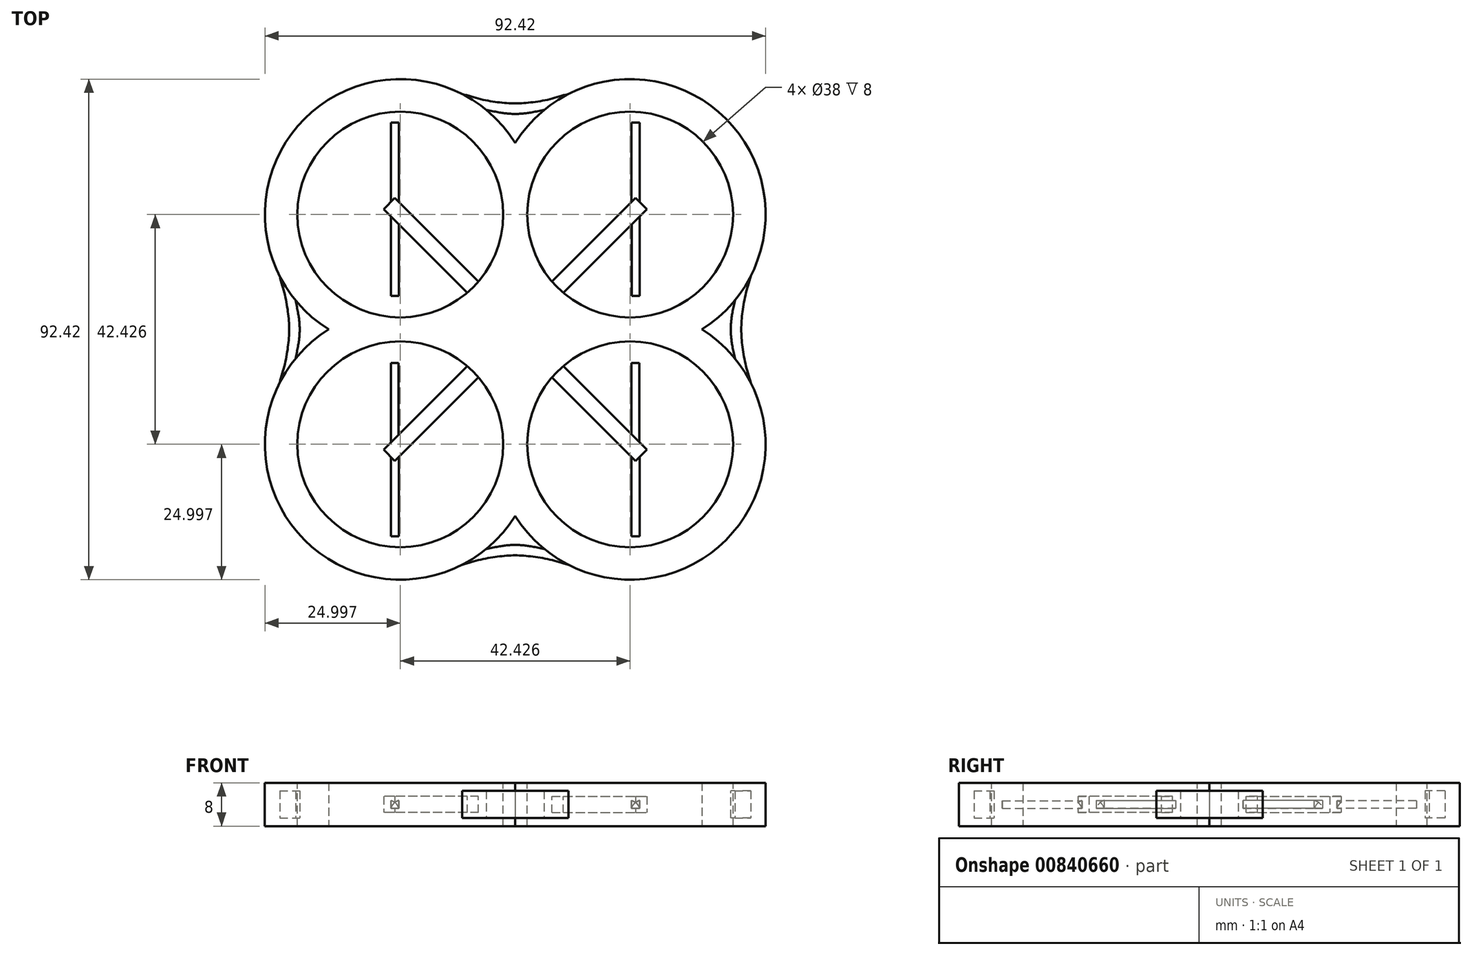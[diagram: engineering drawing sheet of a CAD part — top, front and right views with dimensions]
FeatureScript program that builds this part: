
annotation { "Feature Type Name" : "Feature", "Feature Type Description" : "" }
export const myFeature = defineFeature(function(context is Context, id is Id, definition is map)
    precondition{}
    {
        {
            var Q0;
            Q0=qCreatedBy(makeId("Top.planeOp"),FACE);
            var sketch = newSketch(context, id + "F0", { "sketchPlane" : qUnion([Q0])});
            skLineSegment(sketch, "E0", {"start": v(0, 0) * mm, "end": v(42.43, 42.43) * mm, "construction": true});
            skLineSegment(sketch, "E1", {"start": v(0, 0) * mm, "end": v(21.21, 21.21) * mm});
            skCircle(sketch, "E2", {"center": v(21.21, 21.21) * mm, "radius": 25 * mm});
            skCircle(sketch, "E3.MirrorC", {"center": v(21.21, -21.21) * mm, "radius": 25 * mm});
            skCircle(sketch, "E4.MirrorC", {"center": v(-21.21, 21.21) * mm, "radius": 25 * mm});
            skCircle(sketch, "E5.MirrorC", {"center": v(-21.21, -21.21) * mm, "radius": 25 * mm});
            skSolve(sketch);
        }
        {
            var Q0;
            Q0 = qSketchRegion(id + "F0", true);
            extrude(context, id + "F1", {"entities" : qUnion([Q0]), "endBound" : BoundingType.SYMMETRIC, "depth" : 8 * mm, "offsetDistance" : 25 * mm});
        }
        {
            var Q0;
            Q0=qCreatedBy(makeId("Top.planeOp"),FACE);
            var sketch = newSketch(context, id + "F2", { "sketchPlane" : qUnion([Q0])});
            skLineSegment(sketch, "E6", {"start": v(0, 0) * mm, "end": v(42.43, 42.43) * mm, "construction": true});
            skLineSegment(sketch, "E7", {"start": v(0, 0) * mm, "end": v(21.21, 21.21) * mm});
            skCircle(sketch, "E8", {"center": v(21.21, 21.21) * mm, "radius": 19 * mm});
            skCircle(sketch, "E9.MirrorC", {"center": v(-21.21, 21.21) * mm, "radius": 19 * mm});
            skCircle(sketch, "E10.MirrorC", {"center": v(21.21, -21.21) * mm, "radius": 19 * mm});
            skCircle(sketch, "E11.MirrorC", {"center": v(-21.21, -21.21) * mm, "radius": 19 * mm});
            skSolve(sketch);
        }
        {
            var Q0;
            Q0 = qSketchRegion(id + "F2", true);
            extrude(context, id + "F3", {"entities" : qUnion([Q0]), "operationType" : NewBodyOperationType.REMOVE, "endBound" : BoundingType.SYMMETRIC, "oppositeDirection" : true, "depth" : 25 * mm, "offsetDistance" : 25 * mm});
        }
        {
            var Q0;
            Q0=qCreatedBy(makeId("Top.planeOp"),FACE);
            var sketch = newSketch(context, id + "F4", { "sketchPlane" : qUnion([Q0])});
            skFitSpline(sketch, "E12", {"points": [v(-10.9, 43.62) * mm, v(-7.26, 42.73) * mm, v(-3.36, 41.97) * mm, v(0, 41.72) * mm], "startDerivative": vector(10.52, -0.67) * mm, "endDerivative": vector(9.64, 0) * mm});
            skFitSpline(sketch, "E13", {"points": [v(-6.55, 40.73) * mm, v(-3.36, 40.14) * mm, v(-1.56, 39.87) * mm, v(0, 39.8) * mm], "startDerivative": vector(8.27, -1.19) * mm, "endDerivative": vector(5.4, 0.03) * mm});
            skLineSegment(sketch, "E14", {"start": v(0, 0) * mm, "end": v(31.64, 31.64) * mm, "construction": true});
            skFitSpline(sketch, "E15.MirrorCS", {"points": [v(43.62, -10.9) * mm, v(42.73, -7.26) * mm, v(41.97, -3.36) * mm, v(41.72, 0) * mm], "startDerivative": vector(-0.67, 10.52) * mm, "endDerivative": vector(0, 9.64) * mm});
            skFitSpline(sketch, "E16.MirrorCS", {"points": [v(40.73, -6.55) * mm, v(40.14, -3.36) * mm, v(39.87, -1.56) * mm, v(39.8, 0) * mm], "startDerivative": vector(-1.19, 8.27) * mm, "endDerivative": vector(0.03, 5.4) * mm});
            skFitSpline(sketch, "E17.MirrorCS", {"points": [v(10.9, 43.62) * mm, v(7.26, 42.73) * mm, v(3.36, 41.97) * mm, v(0, 41.72) * mm], "startDerivative": vector(-10.52, -0.67) * mm, "endDerivative": vector(-9.64, 0) * mm});
            skFitSpline(sketch, "E18.MirrorCS", {"points": [v(6.55, 40.73) * mm, v(3.36, 40.14) * mm, v(1.56, 39.87) * mm, v(0, 39.8) * mm], "startDerivative": vector(-8.27, -1.19) * mm, "endDerivative": vector(-5.4, 0.03) * mm});
            skFitSpline(sketch, "E19.MirrorCS", {"points": [v(-43.62, -10.9) * mm, v(-42.73, -7.26) * mm, v(-41.97, -3.36) * mm, v(-41.72, 0) * mm], "startDerivative": vector(0.67, 10.52) * mm, "endDerivative": vector(0, 9.64) * mm});
            skFitSpline(sketch, "E20.MirrorCS", {"points": [v(-40.73, -6.55) * mm, v(-40.14, -3.36) * mm, v(-39.87, -1.56) * mm, v(-39.8, 0) * mm], "startDerivative": vector(1.19, 8.27) * mm, "endDerivative": vector(-0.03, 5.4) * mm});
            skFitSpline(sketch, "E21.MirrorCS", {"points": [v(43.62, 10.9) * mm, v(42.73, 7.26) * mm, v(41.97, 3.36) * mm, v(41.72, 0) * mm], "startDerivative": vector(-0.67, -10.52) * mm, "endDerivative": vector(0, -9.64) * mm});
            skFitSpline(sketch, "E22.MirrorCS", {"points": [v(40.73, 6.55) * mm, v(40.14, 3.36) * mm, v(39.87, 1.56) * mm, v(39.8, 0) * mm], "startDerivative": vector(-1.19, -8.27) * mm, "endDerivative": vector(0.03, -5.4) * mm});
            skFitSpline(sketch, "E23.MirrorCS", {"points": [v(10.9, -43.62) * mm, v(7.26, -42.73) * mm, v(3.36, -41.97) * mm, v(0, -41.72) * mm], "startDerivative": vector(-10.52, 0.67) * mm, "endDerivative": vector(-9.64, 0) * mm});
            skFitSpline(sketch, "E24.MirrorCS", {"points": [v(6.55, -40.73) * mm, v(3.36, -40.14) * mm, v(1.56, -39.87) * mm, v(0, -39.8) * mm], "startDerivative": vector(-8.27, 1.19) * mm, "endDerivative": vector(-5.4, -0.03) * mm});
            skFitSpline(sketch, "E25.MirrorCS", {"points": [v(-10.9, -43.62) * mm, v(-7.26, -42.73) * mm, v(-3.36, -41.97) * mm, v(0, -41.72) * mm], "startDerivative": vector(10.52, 0.67) * mm, "endDerivative": vector(9.64, 0) * mm});
            skFitSpline(sketch, "E26.MirrorCS", {"points": [v(-6.55, -40.73) * mm, v(-3.36, -40.14) * mm, v(-1.56, -39.87) * mm, v(0, -39.8) * mm], "startDerivative": vector(8.27, 1.19) * mm, "endDerivative": vector(5.4, -0.03) * mm});
            skFitSpline(sketch, "E27.MirrorCS", {"points": [v(-40.73, 6.55) * mm, v(-40.14, 3.36) * mm, v(-39.87, 1.56) * mm, v(-39.8, 0) * mm], "startDerivative": vector(1.19, -8.27) * mm, "endDerivative": vector(-0.03, -5.4) * mm});
            skFitSpline(sketch, "E28.MirrorCS", {"points": [v(-43.62, 10.9) * mm, v(-42.73, 7.26) * mm, v(-41.97, 3.36) * mm, v(-41.72, 0) * mm], "startDerivative": vector(0.67, -10.52) * mm, "endDerivative": vector(0, -9.64) * mm});
            skLineSegment(sketch, "E29", {"start": v(-43.62, 10.9) * mm, "end": v(-40.73, 6.55) * mm});
            skLineSegment(sketch, "E30", {"start": v(-40.73, -6.55) * mm, "end": v(-43.62, -10.9) * mm});
            skLineSegment(sketch, "E31", {"start": v(-10.9, 43.62) * mm, "end": v(-6.55, 40.73) * mm});
            skLineSegment(sketch, "E32", {"start": v(10.9, 43.62) * mm, "end": v(6.55, 40.73) * mm});
            skLineSegment(sketch, "E33", {"start": v(-6.55, -40.73) * mm, "end": v(-10.9, -43.62) * mm});
            skLineSegment(sketch, "E34", {"start": v(6.55, -40.73) * mm, "end": v(10.9, -43.62) * mm});
            skLineSegment(sketch, "E35", {"start": v(43.62, -10.9) * mm, "end": v(40.73, -6.55) * mm});
            skLineSegment(sketch, "E36", {"start": v(43.62, 10.9) * mm, "end": v(40.73, 6.55) * mm});
            skSolve(sketch);
        }
        {
            var Q0;
            Q0 = qSketchRegion(id + "F4", true);
            extrude(context, id + "F5", {"entities" : qUnion([Q0]), "operationType" : NewBodyOperationType.ADD, "endBound" : BoundingType.SYMMETRIC, "depth" : 5 * mm, "offsetDistance" : 25 * mm});
        }
        {
            var Q0;
            Q0=qCreatedBy(makeId("Top.planeOp"),FACE);
            var sketch = newSketch(context, id + "F6", { "sketchPlane" : qUnion([Q0])});
            skFitSpline(sketch, "E37", {"points": [v(0, 21.62) * mm, v(-3.08, 14.95) * mm, v(-6.05, 8.7) * mm, v(-9.09, 0) * mm], "startDerivative": vector(-14.1, -3.44) * mm, "endDerivative": vector(-1.81, -25) * mm});
            skFitSpline(sketch, "E38.MirrorCS", {"points": [v(0, 21.62) * mm, v(3.08, 14.95) * mm, v(6.05, 8.7) * mm, v(9.09, 0) * mm], "startDerivative": vector(14.1, -3.44) * mm, "endDerivative": vector(1.81, -25) * mm});
            skFitSpline(sketch, "E39.MirrorCS", {"points": [v(0, -21.62) * mm, v(-3.08, -14.95) * mm, v(-6.05, -8.7) * mm, v(-9.09, 0) * mm], "startDerivative": vector(-14.1, 3.44) * mm, "endDerivative": vector(-1.81, 25) * mm});
            skFitSpline(sketch, "E40.MirrorCS", {"points": [v(0, -21.62) * mm, v(3.08, -14.95) * mm, v(6.05, -8.7) * mm, v(9.09, 0) * mm], "startDerivative": vector(14.1, 3.44) * mm, "endDerivative": vector(1.81, 25) * mm});
            skSolve(sketch);
        }
        {
            var Q0;
            Q0 = qSketchRegion(id + "F6", true);
            extrude(context, id + "F7", {"entities" : qUnion([Q0]), "operationType" : NewBodyOperationType.ADD, "endBound" : BoundingType.SYMMETRIC, "depth" : 8 * mm, "offsetDistance" : 25 * mm});
        }
        {
            var Q0;
            Q0=qCreatedBy(makeId("Top.planeOp"),FACE);
            var sketch = newSketch(context, id + "F8", { "sketchPlane" : qUnion([Q0])});
            skLineSegment(sketch, "E41", {"start": v(-2.07, 0) * mm, "end": v(-23.29, 21.21) * mm});
            skLineSegment(sketch, "E42", {"start": v(0, 0) * mm, "end": v(-42.43, 42.43) * mm, "construction": true});
            skLineSegment(sketch, "E43.MirrorCS", {"start": v(0, 2.07) * mm, "end": v(-21.21, 23.29) * mm});
            skLineSegment(sketch, "E44.MirrorCS", {"start": v(0, 2.07) * mm, "end": v(21.21, 23.29) * mm});
            skLineSegment(sketch, "E45.MirrorCS", {"start": v(2.07, 0) * mm, "end": v(23.29, 21.21) * mm});
            skLineSegment(sketch, "E46.MirrorCS", {"start": v(2.07, 0) * mm, "end": v(23.29, -21.21) * mm});
            skLineSegment(sketch, "E47.MirrorCS", {"start": v(0, -2.07) * mm, "end": v(21.21, -23.29) * mm});
            skLineSegment(sketch, "E48.MirrorCS", {"start": v(-2.07, 0) * mm, "end": v(-23.29, -21.21) * mm});
            skLineSegment(sketch, "E49.MirrorCS", {"start": v(0, -2.07) * mm, "end": v(-21.21, -23.29) * mm});
            skLineSegment(sketch, "E50", {"start": v(2.07, 0) * mm, "end": v(23.21, 21.14) * mm});
            skLineSegment(sketch, "E51", {"start": v(21.21, 23.29) * mm, "end": v(23.21, 21.14) * mm});
            skLineSegment(sketch, "E52.MirrorCS", {"start": v(-21.21, 23.29) * mm, "end": v(-23.21, 21.14) * mm});
            skLineSegment(sketch, "E53.MirrorCS", {"start": v(0, 0) * mm, "end": v(-42.43, -42.43) * mm, "construction": true});
            skLineSegment(sketch, "E54.MirrorCS", {"start": v(-21.21, -23.29) * mm, "end": v(-23.21, -21.14) * mm});
            skLineSegment(sketch, "E55.MirrorCS", {"start": v(21.21, -23.29) * mm, "end": v(23.21, -21.14) * mm});
            skLineSegment(sketch, "E56", {"start": v(23.21, -21.14) * mm, "end": v(21.21, -23.29) * mm});
            skLineSegment(sketch, "E57", {"start": v(-23.21, -21.14) * mm, "end": v(-21.21, -23.29) * mm});
            skLineSegment(sketch, "E58", {"start": v(0, 2.07) * mm, "end": v(-22.21, 24.29) * mm});
            skPoint(sketch, "E58.endSnap0", {"position": v(-22.21, 22.21) * mm});
            skLineSegment(sketch, "E59.MirrorCS", {"start": v(-2.07, 0) * mm, "end": v(-24.29, 22.21) * mm});
            skLineSegment(sketch, "E60.MirrorCS", {"start": v(0, 2.07) * mm, "end": v(22.21, 24.29) * mm});
            skLineSegment(sketch, "E61.MirrorCS", {"start": v(2.07, 0) * mm, "end": v(24.29, 22.21) * mm});
            skLineSegment(sketch, "E62.MirrorCS", {"start": v(0, -2.07) * mm, "end": v(-22.21, -24.29) * mm});
            skLineSegment(sketch, "E63.MirrorCS", {"start": v(-2.07, 0) * mm, "end": v(-24.29, -22.21) * mm});
            skLineSegment(sketch, "E64.MirrorCS", {"start": v(2.07, 0) * mm, "end": v(24.29, -22.21) * mm});
            skLineSegment(sketch, "E65.MirrorCS", {"start": v(0, -2.07) * mm, "end": v(22.21, -24.29) * mm});
            skLineSegment(sketch, "E66", {"start": v(0, 2.07) * mm, "end": v(-20.14, 22.21) * mm});
            skLineSegment(sketch, "E67", {"start": v(-20.14, 22.21) * mm, "end": v(-22.21, 20.14) * mm});
            skLineSegment(sketch, "E68", {"start": v(-22.21, 20.14) * mm, "end": v(-22.21, 24.29) * mm});
            skLineSegment(sketch, "E69", {"start": v(-22.21, 24.29) * mm, "end": v(-24.29, 22.21) * mm});
            skLineSegment(sketch, "E70", {"start": v(-24.29, 22.21) * mm, "end": v(-20.14, 22.21) * mm});
            skLineSegment(sketch, "E71.MirrorCS", {"start": v(22.21, 24.29) * mm, "end": v(24.29, 22.21) * mm});
            skLineSegment(sketch, "E72.MirrorCS", {"start": v(20.14, 22.21) * mm, "end": v(22.21, 20.14) * mm});
            skLineSegment(sketch, "E73.MirrorCS", {"start": v(22.21, 20.14) * mm, "end": v(22.21, 24.29) * mm});
            skLineSegment(sketch, "E74.MirrorCS", {"start": v(24.29, 22.21) * mm, "end": v(20.14, 22.21) * mm});
            skPoint(sketch, "E75", {"position": v(22.21, 22.21) * mm});
            skLineSegment(sketch, "E76.MirrorCS", {"start": v(22.21, -20.14) * mm, "end": v(22.21, -24.29) * mm});
            skLineSegment(sketch, "E77.MirrorCS", {"start": v(24.29, -22.21) * mm, "end": v(20.14, -22.21) * mm});
            skPoint(sketch, "E78.MirrorP", {"position": v(22.21, -22.21) * mm});
            skLineSegment(sketch, "E79.MirrorCS", {"start": v(22.21, -24.29) * mm, "end": v(24.29, -22.21) * mm});
            skLineSegment(sketch, "E80.MirrorCS", {"start": v(20.14, -22.21) * mm, "end": v(22.21, -20.14) * mm});
            skLineSegment(sketch, "E81.MirrorCS", {"start": v(-20.14, -22.21) * mm, "end": v(-22.21, -20.14) * mm});
            skLineSegment(sketch, "E82.MirrorCS", {"start": v(-22.21, -24.29) * mm, "end": v(-24.29, -22.21) * mm});
            skLineSegment(sketch, "E83.MirrorCS", {"start": v(-24.29, -22.21) * mm, "end": v(-20.14, -22.21) * mm});
            skLineSegment(sketch, "E84.MirrorCS", {"start": v(-22.21, -20.14) * mm, "end": v(-22.21, -24.29) * mm});
            skPoint(sketch, "E85.MirrorP", {"position": v(-22.21, -22.21) * mm});
            skSolve(sketch);
        }
        {
            var Q0;
            Q0 = qSketchRegion(id + "F8", true);
            extrude(context, id + "F9", {"entities" : qUnion([Q0]), "operationType" : NewBodyOperationType.ADD, "endBound" : BoundingType.SYMMETRIC, "depth" : 3 * mm, "offsetDistance" : 25 * mm});
        }
        {
            var Q0;
            Q0=qCreatedBy(makeId("Top.planeOp"),FACE);
            var sketch = newSketch(context, id + "F10", { "sketchPlane" : qUnion([Q0])});
            skLineSegment(sketch, "E86.bottom", {"start": v(-22.96, 38.21) * mm, "end": v(-21.46, 38.21) * mm});
            skLineSegment(sketch, "E86.top", {"start": v(-22.96, 6.21) * mm, "end": v(-21.46, 6.21) * mm});
            skLineSegment(sketch, "E86.left", {"start": v(-22.96, 38.21) * mm, "end": v(-22.96, 6.21) * mm});
            skLineSegment(sketch, "E86.right", {"start": v(-21.46, 38.21) * mm, "end": v(-21.46, 6.21) * mm});
            skPoint(sketch, "E86.middle", {"position": v(-22.21, 22.21) * mm});
            skLineSegment(sketch, "E87.MirrorCS", {"start": v(21.46, 38.21) * mm, "end": v(21.46, 6.21) * mm});
            skLineSegment(sketch, "E88.MirrorCS", {"start": v(22.96, 38.21) * mm, "end": v(22.96, 6.21) * mm});
            skLineSegment(sketch, "E89.MirrorCS", {"start": v(22.96, 38.21) * mm, "end": v(21.46, 38.21) * mm});
            skLineSegment(sketch, "E90.MirrorCS", {"start": v(22.96, 6.21) * mm, "end": v(21.46, 6.21) * mm});
            skLineSegment(sketch, "E91.MirrorCS", {"start": v(-22.96, -38.21) * mm, "end": v(-22.96, -6.21) * mm});
            skLineSegment(sketch, "E92.MirrorCS", {"start": v(-21.46, -38.21) * mm, "end": v(-21.46, -6.21) * mm});
            skLineSegment(sketch, "E93.MirrorCS", {"start": v(-22.96, -6.21) * mm, "end": v(-21.46, -6.21) * mm});
            skLineSegment(sketch, "E94.MirrorCS", {"start": v(-22.96, -38.21) * mm, "end": v(-21.46, -38.21) * mm});
            skLineSegment(sketch, "E95.MirrorCS", {"start": v(22.96, -38.21) * mm, "end": v(21.46, -38.21) * mm});
            skLineSegment(sketch, "E96.MirrorCS", {"start": v(22.96, -6.21) * mm, "end": v(21.46, -6.21) * mm});
            skLineSegment(sketch, "E97.MirrorCS", {"start": v(21.46, -38.21) * mm, "end": v(21.46, -6.21) * mm});
            skLineSegment(sketch, "E98.MirrorCS", {"start": v(22.96, -38.21) * mm, "end": v(22.96, -6.21) * mm});
            skSolve(sketch);
        }
        {
            var Q0;
            Q0 = qSketchRegion(id + "F10", true);
            extrude(context, id + "F11", {"entities" : qUnion([Q0]), "operationType" : NewBodyOperationType.ADD, "endBound" : BoundingType.SYMMETRIC, "depth" : 1.5 * mm, "offsetDistance" : 25 * mm});
        }
        {
            var Q0;
            {var subQ1=sQuery(id+"F10.wireOp",EDGE,"E88.MirrorCS");Q0=makeQuery(id+"F11.boolean.opBoolean","SPLIT",EDGE,{"disambiguationData":[TD([makeQuery(id+"F9.opExtrude","SWEPT_FACE",FACE,{"disambiguationData":[OSD([sQuery(id+"F8.wireOp",EDGE,"E71.MirrorCS")])]})])],"derivedFrom":makeQuery(id+"F11.opExtrude","CAP_EDGE",EDGE,{"disambiguationData":[OSD([subQ1])],"isStart":false})});}
            var Q1;
            {var subQ0=sQuery(id+"F10.wireOp",EDGE,"E87.MirrorCS");Q1=makeQuery(id+"F11.boolean.opBoolean","SPLIT",EDGE,{"disambiguationData":[TD([makeQuery(id+"F9.opExtrude","SWEPT_FACE",FACE,{"disambiguationData":[OSD([sQuery(id+"F8.wireOp",EDGE,"E61.MirrorCS")])]})])],"derivedFrom":makeQuery(id+"F11.opExtrude","CAP_EDGE",EDGE,{"disambiguationData":[OSD([subQ0])],"isStart":false})});}
            var Q2;
            {var subQ0=sQuery(id+"F10.wireOp",EDGE,"E86.bottom");var subQ1=sQuery(id+"F10.wireOp",EDGE,"E86.right");Q2=makeQuery(id+"F11.boolean.opBoolean","SPLIT",EDGE,{"disambiguationData":[TD([makeQuery(id+"F11.opExtrude","SWEPT_FACE",FACE,{"disambiguationData":[OSD([subQ0])]})])],"derivedFrom":makeQuery(id+"F11.opExtrude","CAP_EDGE",EDGE,{"disambiguationData":[OSD([subQ1])],"isStart":false})});}
            var Q3;
            {var subQ0=sQuery(id+"F10.wireOp",EDGE,"E86.left");Q3=makeQuery(id+"F11.boolean.opBoolean","SPLIT",EDGE,{"disambiguationData":[TD([makeQuery(id+"F9.opExtrude","SWEPT_FACE",FACE,{"disambiguationData":[OSD([sQuery(id+"F8.wireOp",EDGE,"E59.MirrorCS")])]})])],"derivedFrom":makeQuery(id+"F11.opExtrude","CAP_EDGE",EDGE,{"disambiguationData":[OSD([subQ0])],"isStart":false})});}
            var Q4;
            {var subQ1=sQuery(id+"F10.wireOp",EDGE,"E92.MirrorCS");Q4=makeQuery(id+"F11.boolean.opBoolean","SPLIT",EDGE,{"disambiguationData":[TD([makeQuery(id+"F9.opExtrude","SWEPT_FACE",FACE,{"disambiguationData":[OSD([sQuery(id+"F8.wireOp",EDGE,"E63.MirrorCS")])]})])],"derivedFrom":makeQuery(id+"F11.opExtrude","CAP_EDGE",EDGE,{"disambiguationData":[OSD([subQ1])],"isStart":false})});}
            var Q5;
            {var subQ1=sQuery(id+"F10.wireOp",EDGE,"E91.MirrorCS");Q5=makeQuery(id+"F11.boolean.opBoolean","SPLIT",EDGE,{"disambiguationData":[TD([makeQuery(id+"F9.opExtrude","SWEPT_FACE",FACE,{"disambiguationData":[OSD([sQuery(id+"F8.wireOp",EDGE,"E82.MirrorCS")])]})])],"derivedFrom":makeQuery(id+"F11.opExtrude","CAP_EDGE",EDGE,{"disambiguationData":[OSD([subQ1])],"isStart":false})});}
            var Q6;
            {var subQ0=sQuery(id+"F10.wireOp",EDGE,"E98.MirrorCS");Q6=makeQuery(id+"F11.boolean.opBoolean","SPLIT",EDGE,{"disambiguationData":[TD([makeQuery(id+"F9.opExtrude","SWEPT_FACE",FACE,{"disambiguationData":[OSD([sQuery(id+"F8.wireOp",EDGE,"E64.MirrorCS")])]})])],"derivedFrom":makeQuery(id+"F11.opExtrude","CAP_EDGE",EDGE,{"disambiguationData":[OSD([subQ0])],"isStart":false})});}
            var Q7;
            {var subQ0=sQuery(id+"F10.wireOp",EDGE,"E97.MirrorCS");Q7=makeQuery(id+"F11.boolean.opBoolean","SPLIT",EDGE,{"disambiguationData":[TD([makeQuery(id+"F9.opExtrude","SWEPT_FACE",FACE,{"disambiguationData":[OSD([sQuery(id+"F8.wireOp",EDGE,"E65.MirrorCS")])]})])],"derivedFrom":makeQuery(id+"F11.opExtrude","CAP_EDGE",EDGE,{"disambiguationData":[OSD([subQ0])],"isStart":false})});}
            fillet(context, id + "F12", {"entities" : qUnion([Q0, Q1, Q2, Q3, Q4, Q5, Q6, Q7]), "radius" : 2 * mm, "tangentPropagation" : true, "allowEdgeOverflow" : false});
        }
    });
